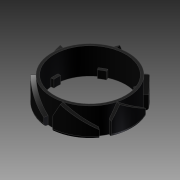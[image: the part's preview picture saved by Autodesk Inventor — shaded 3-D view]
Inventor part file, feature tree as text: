
AUTODESK INVENTOR PART (.ipt)
format: ipt  version: 2012 (Build 160160000, 160)  size: 272,896 bytes
history: native  units: mm
features: sketch x5, extrude x3, pattern_circular x3, helix x2, fillet x1, mirror x1
ambient origin geometry x8: Origin, YZ Plane, XZ Plane, XY Plane, X Axis, Y Axis, Z Axis, Center Point
bodies: Solid1 (feature_tree)
feature tree (15):
  sketch  "Sketch1"  dims[d0=64.0mm d1=54.2mm d2=50.0mm]
  extrude  "Extrusion2"  Depth=54.2mm
  sketch  "Sketch3"  dims[d3=58.0mm d6=20.0mm d7=0.0mm]
  fillet  "Fillet3"  Radius=50.0mm
  sketch  "Sketch5"  dims[d10=4.0mm]
  extrude  "Extrusion9"  Depth=20.0mm TaperAngle=0.0deg
  pattern_circular  "Circular Pattern6"  [2 undecoded]
  sketch  "Sketch7"  dims[d17=2.0mm]
  helix  "Coil5"  [1 undecoded]
  helix  "Coil6"  [1 undecoded]
  pattern_circular  "Circular Pattern7"  [2 undecoded]
  extrude  "Extrusion11"  Depth=10.0mm TaperAngle=0.0deg
  mirror  "Mirror5"
  pattern_circular  "Circular Pattern8"  Count=6 Angle=360.0deg
  sketch  "Sketch9"  dims[d35=40.1mm d36=49.0mm d37=1.012291mm d46=2.0mm d47=4.0mm d58=4.0mm d59=26.0mm d86=2.094395mm d87=10.0mm d88=0.0mm d89=60.0mm d90=360.0deg d92=1.047198mm d93=29.0mm d94=22.0mm d95=10.0mm d96=16.0mm d97=1.25mm d98=0.0mm d99=90.0deg d100=90.0deg d101=0.0mm d102=0.0mm d103=16.0mm d104=10.0mm d105=16.0mm d106=0.416667mm d107=0.0mm d108=90.0deg d109=90.0deg d110=0.0mm d111=0.0mm d112=60.0mm d113=360.0deg d115=18.0mm d127=1.012291mm d128=30.0deg d129=50.1mm d130=55.0mm d131=5.8mm d132=0.0mm d133=60.0mm d134=360.0deg]
note: 6 required parameter values undecoded (feature->parameter linkage not recoverable at this tier; creation-order binding heuristic only, values carry confidence <= 0.55)
